# Revit family: Seating-LAMMHULTS-GRADE-Sledbased
name_source: partatom
category: Furniture
revit_build: Autodesk Revit 2014 (Build: 20140709_2115(x64)
units: mm (PartAtom-declared; Revit-internal decimal feet)

## types (3) — shared parameters
Assembly Code = E2020
Depth = 780 mm  [stored 2.55906 ft]
Description = *Please enter mtrl description here for use in mto*
Height = 540 mm  [stored 1.77165 ft]
Keynote = 46.B
Manufacturer = LAMMHULTS
Model = GRADE
URL = www.lammhults.se
Weight = 4.5
Width = 530 mm  [stored 1.73885 ft]

## per-type parameters (varying)
| type | Frame Material | Seat Material | Seat Pad Material |
| Chrome - White | Metal - Chrome - Polished | Colour - Coated - White | Fabric - Divina 3 - 236 |
| Coated - Pistachio | Colour - Coated - Pistachio | Colour - Coated - Pistachio | Fabric - Divina 3 - 384 |
| Coated - Black | Colour - Coated - Black | Colour - Coated - Black | Fabric - Divina 3 - 691 |

note: [stored X ft] marks values corroborated as IEEE doubles in the binary element streams (Revit-internal decimal feet)

## geometry (parser evidence)
native form markers: Blend x417, Sweep x1
no freeform markers — native parametric forms only
